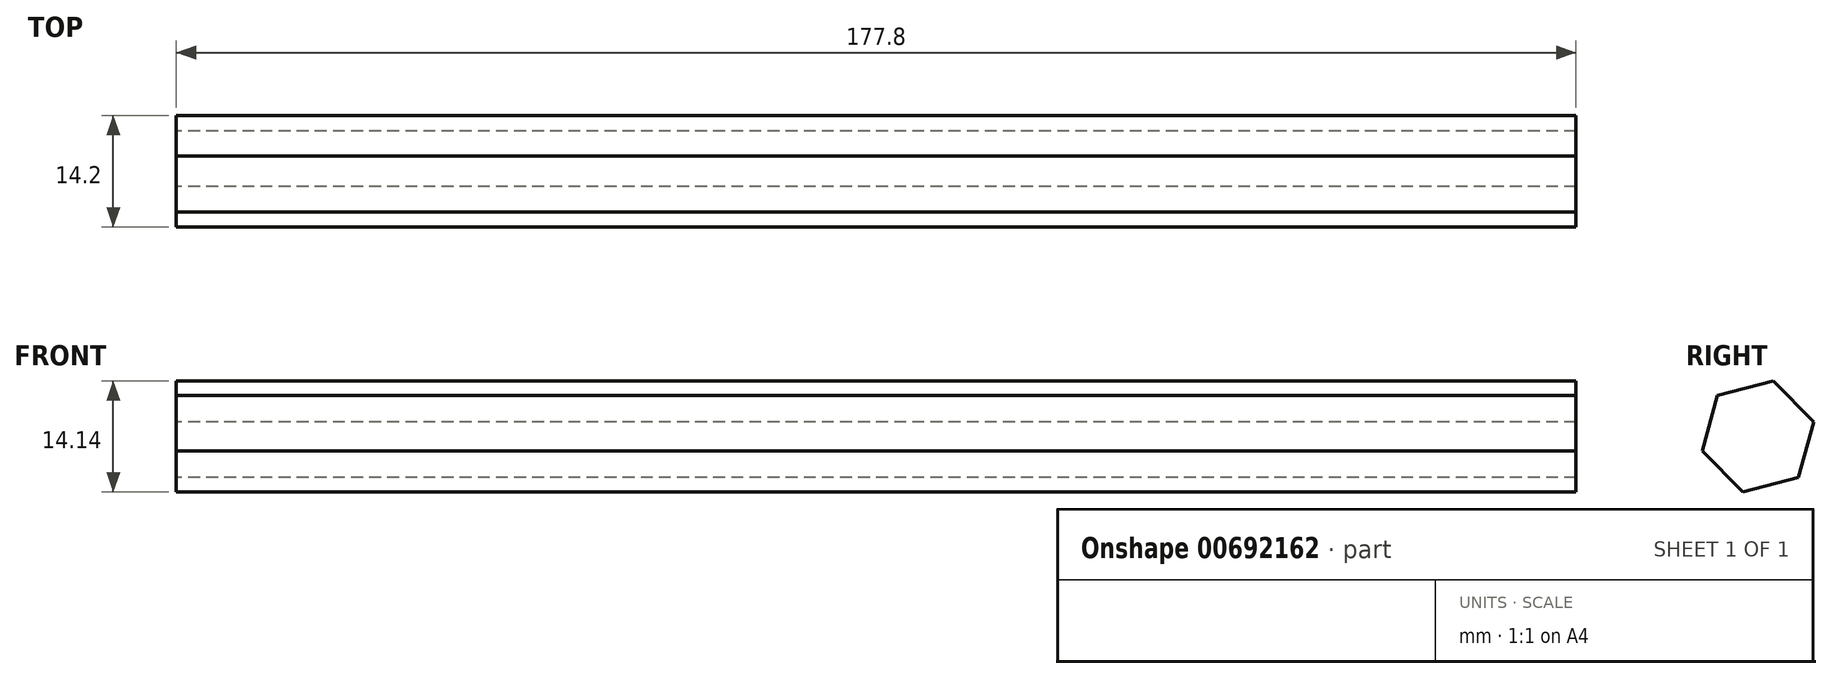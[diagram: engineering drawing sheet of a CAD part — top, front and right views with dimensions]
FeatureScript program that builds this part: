
annotation { "Feature Type Name" : "Feature", "Feature Type Description" : "" }
export const myFeature = defineFeature(function(context is Context, id is Id, definition is map)
    precondition{}
    {
        {
            var Q0;
            Q0=qCreatedBy(makeId("Right.planeOp"),FACE);
            var sketch = newSketch(context, id + "F0", { "sketchPlane" : qUnion([Q0])});
            skCircle(sketch, "E0", {"center": v(0, 0) * mm, "radius": 6.35 * mm, "construction": true});
            skLineSegment(sketch, "E1.0", {"start": v(7.1, 1.85) * mm, "end": v(5.15, -5.22) * mm});
            skLineSegment(sketch, "E1.1", {"start": v(5.15, -5.22) * mm, "end": v(-1.95, -7.07) * mm});
            skLineSegment(sketch, "E1.2", {"start": v(-1.95, -7.07) * mm, "end": v(-7.1, -1.85) * mm});
            skLineSegment(sketch, "E1.3", {"start": v(-7.1, -1.85) * mm, "end": v(-5.15, 5.22) * mm});
            skLineSegment(sketch, "E1.4", {"start": v(-5.15, 5.22) * mm, "end": v(1.95, 7.07) * mm});
            skLineSegment(sketch, "E1.5", {"start": v(1.95, 7.07) * mm, "end": v(7.1, 1.85) * mm});
            skPoint(sketch, "E1.0.midPoint", {"position": v(6.12, -1.68) * mm});
            skSolve(sketch);
        }
        {
            var Q0;
            Q0 = qSketchRegion(id + "F0", true);
            extrude(context, id + "F1", {"entities" : qUnion([Q0]), "depth" : 177.8 * mm, "offsetDistance" : 25.4 * mm});
        }
    });
